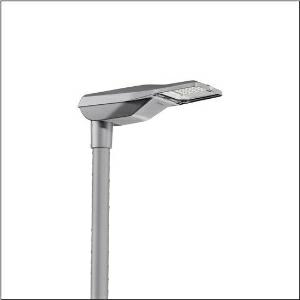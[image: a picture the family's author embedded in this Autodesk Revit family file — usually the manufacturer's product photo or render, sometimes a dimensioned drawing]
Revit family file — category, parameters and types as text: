
# Revit family: streetlight_sl_21_iq_micro___stw1_0a_5xe1e21g08cb_2b52
name_source: partatom
category: Lighting Fixtures
units: mm (PartAtom-declared; Revit-internal decimal feet)

## family parameters
Cut with Voids When Loaded = No
Host = Face
Light Source = No
Part Type = Normal
Room Calculation Point = No
Round Connector Dimension = Use Diameter
Shared = No

## types (1)
- --- (1 x LED, 2380 lm, 19.4 W, 2200K)
    Apparent Load = 19 VA
    CIE Flux Codes = 38 75 98 100 100
    Color Rendering = 70
    Color Temperature = 2200K
    Default Elevation = 1800 mm
    Description = Streetlight SL 21 iQ micro, mast luminaire, primary light control with lens, of PMMA, primary optical cover: cover, of toughened safety glass, transparent, light distribution: STW1.0a, light emission: direct distribution, primary light characteristic: asymmetric, installation type: post-top, side-entry, LED, High Power LED, rated luminous flux: 2.380lm, luminous efficacy: 123lm/W, light colour: 722, colour temperature: 2200K, control gear: iQ Street-Remote, control: Street-Remote, Auto-Match, Temp-Guard, Lumen-Switch, Night-Set, Smart-Wire, Light-Fading, Desk-Remote (wireless, voltage-free reading and setting of iQ features in the workshop via application-optimized NFC function/RFID function), optimised constant luminous flux control (CLO 2.0), pre-setting: linear dimming characteristic, mains connection: 220..240V, AC, 50/60Hz, start of lifetime: 19W, end of service life: 20W, reduction: 10W, luminaire housing, of diecast aluminium, powder-coated, Siteco® metallic grey (DB 702S), corrosivity category C5 mid according to DIN EN ISO 12944, please order mast flange separately, inclination adjustable: 0°, 5°, 10°, 15°, sealing non-destructively replaceable, multi-level sealing system, length: 528mm, width: 235mm, height: 110mm, mast flange for spigot size: 42mm (side-entry): 5XC10008XM4, 60/48mm (side-entry/post-top): 5XC10108XM2, 76/60mm (side-entry/post-top): 5XC10108XM1, protection rating (complete): IP66, insulation class (complete): insulation class II (safety insulation), certification: CE, ENEC, ENEC+, VDE, impact resistance: IK10, permissible operating ambient temperature for outdoor applications: -40..+50°C, standard-compliant lighting for roads and squares, packaging unit: 1 piece

Light Distribution: STW1.0a
    Height = 110 mm
    Lamp = 1 x LED
    Lamp Light Flux = 2380 lm
    Lamp Power = 19.4 W
    Lamp count = 1
    Length = 528 mm
    Luminous efficacy = 123 lm/W
    Manufacturer = Siteco
    ModVariant = No
    Model = 5XE1E21G08CB
    Number of Poles = 1
    OnlyDefault = Yes
    Power Factor = 1
    Product Name = Streetlight SL 21 iQ micro | STW1.0a
    Product group = mast luminaire | pylon top
    ProductGroupID = 6100
    Protection Class = Protection class II
    Protection Degree = IP 66
    RLX_Detail_Level = 1
    RLX_Emergency_Light_Flux = 0 lm
    RLX_Emergency_Type = 0
    RLX_Emergency_Type_DB = No
    RlxData = <blob elided: 98401 chars, md5=53ebc873>
    Socket = socket
    Standby Power = 0 W
    System Light Flux = 2380 lm
    System Power = 19 W
    Type Comments = factory setting: luminous flux: 100 % | dim-lin: 254 | 387 mA
    Type Image = l_1006881.jpg
    URL = http://relux.com
    VarID = @adj_138932
    Voltage = 0 V
    Weight = 0.00 kg
    Width = 235 mm

## geometry (parser evidence)
native form markers: Blend x4, Sweep x9
no freeform markers — native parametric forms only
